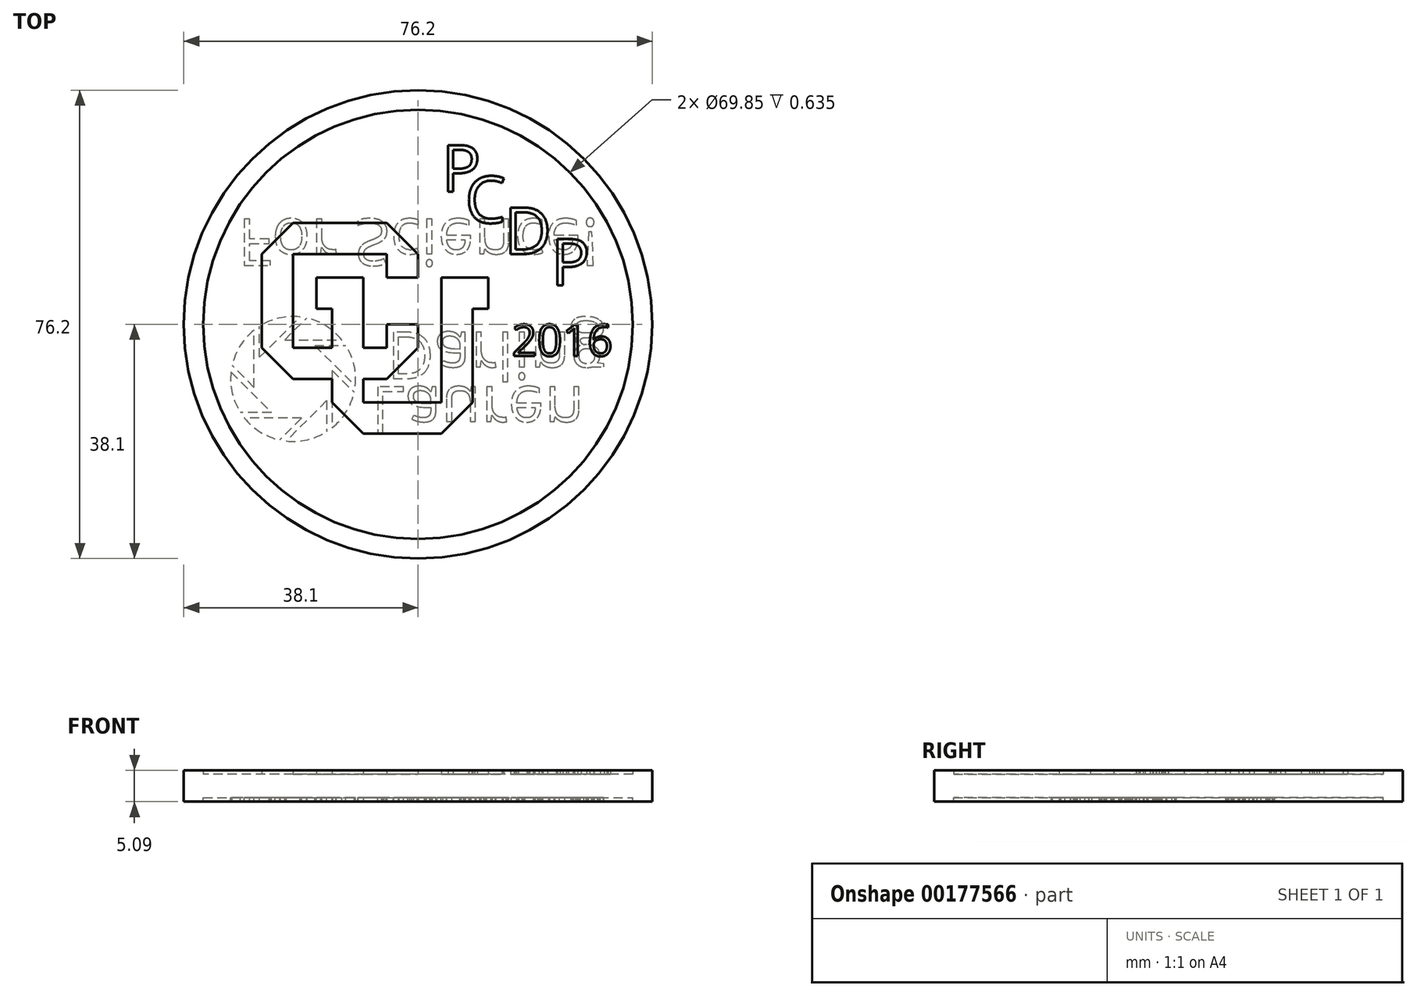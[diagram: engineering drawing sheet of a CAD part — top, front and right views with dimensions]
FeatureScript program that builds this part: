
annotation { "Feature Type Name" : "Feature", "Feature Type Description" : "" }
export const myFeature = defineFeature(function(context is Context, id is Id, definition is map)
    precondition{}
    {
        {
            var Q0;
            Q0=qCreatedBy(makeId("Top.planeOp"),FACE);
            var sketch = newSketch(context, id + "F0", { "sketchPlane" : qUnion([Q0])});
            skCircle(sketch, "E0", {"center": v(0, 0) * mm, "radius": 38.1 * mm});
            skSolve(sketch);
        }
        {
            var Q0;
            Q0 = qSketchRegion(id + "F0", true);
            extrude(context, id + "F1", {"entities" : qUnion([Q0]), "depth" : 3.8 * mm});
        }
        {
            var Q0;
            Q0=makeQuery(id+"F1.opExtrude","CAP_FACE",FACE,{"disambiguationData":[OSD([sQuery(id+"F0.wireOp",EDGE,"E0")])],"isStart":false});
            var sketch = newSketch(context, id + "F2", { "sketchPlane" : qUnion([Q0])});
            skCircle(sketch, "E1", {"center": v(0, 0) * mm, "radius": 38.1 * mm});
            skCircle(sketch, "E2", {"center": v(0, 0) * mm, "radius": 34.93 * mm});
            skLineSegment(sketch, "E3", {"start": v(0, 0) * mm, "end": v(0, -3.81) * mm});
            skLineSegment(sketch, "E4", {"start": v(0, -3.81) * mm, "end": v(-5.08, -8.9) * mm});
            skLineSegment(sketch, "E5", {"start": v(-5.08, -8.89) * mm, "end": v(-8.9, -8.89) * mm});
            skLineSegment(sketch, "E6", {"start": v(-20.32, -8.9) * mm, "end": v(-25.4, -3.8) * mm});
            skLineSegment(sketch, "E7", {"start": v(-25.4, -3.81) * mm, "end": v(-25.4, 11.43) * mm});
            skLineSegment(sketch, "E8", {"start": v(-25.4, 11.43) * mm, "end": v(-20.32, 16.51) * mm});
            skLineSegment(sketch, "E9", {"start": v(-20.32, 16.5) * mm, "end": v(-5.08, 16.51) * mm});
            skLineSegment(sketch, "E10", {"start": v(-5.08, 16.51) * mm, "end": v(0, 11.43) * mm});
            skLineSegment(sketch, "E11", {"start": v(0, 11.43) * mm, "end": v(0, 7.62) * mm});
            skLineSegment(sketch, "E12", {"start": v(0, 7.62) * mm, "end": v(-5.08, 7.62) * mm});
            skLineSegment(sketch, "E13", {"start": v(-5.08, 7.62) * mm, "end": v(-5.08, 11.43) * mm});
            skLineSegment(sketch, "E14", {"start": v(-5.08, 11.43) * mm, "end": v(-20.32, 11.43) * mm});
            skLineSegment(sketch, "E15", {"start": v(-20.32, 11.43) * mm, "end": v(-20.32, -3.81) * mm});
            skLineSegment(sketch, "E16", {"start": v(-20.32, -3.81) * mm, "end": v(-13.97, -3.81) * mm});
            skLineSegment(sketch, "E17", {"start": v(-5.08, -3.81) * mm, "end": v(-5.08, 0) * mm});
            skLineSegment(sketch, "E18", {"start": v(-5.08, 0) * mm, "end": v(0, 0) * mm});
            skLineSegment(sketch, "E19", {"start": v(-8.9, -3.81) * mm, "end": v(-8.9, 7.62) * mm});
            skLineSegment(sketch, "E20", {"start": v(-8.9, 7.62) * mm, "end": v(-16.51, 7.62) * mm});
            skLineSegment(sketch, "E21", {"start": v(-16.51, 7.62) * mm, "end": v(-16.51, 2.54) * mm});
            skLineSegment(sketch, "E22", {"start": v(-16.51, 2.54) * mm, "end": v(-13.97, 2.54) * mm});
            skLineSegment(sketch, "E23", {"start": v(-13.97, 2.54) * mm, "end": v(-13.97, -3.81) * mm});
            skLineSegment(sketch, "E24", {"start": v(-13.97, -8.9) * mm, "end": v(-13.97, -12.7) * mm});
            skLineSegment(sketch, "E25", {"start": v(-13.97, -12.7) * mm, "end": v(-8.89, -17.78) * mm});
            skLineSegment(sketch, "E26", {"start": v(-8.9, -17.78) * mm, "end": v(3.8, -17.78) * mm});
            skLineSegment(sketch, "E27", {"start": v(3.8, -17.78) * mm, "end": v(8.9, -12.7) * mm});
            skLineSegment(sketch, "E28", {"start": v(8.9, -12.7) * mm, "end": v(8.9, 2.54) * mm});
            skLineSegment(sketch, "E29", {"start": v(8.9, 2.54) * mm, "end": v(11.43, 2.54) * mm});
            skLineSegment(sketch, "E30", {"start": v(11.43, 2.54) * mm, "end": v(11.43, 7.62) * mm});
            skLineSegment(sketch, "E31", {"start": v(11.43, 7.62) * mm, "end": v(3.8, 7.62) * mm});
            skLineSegment(sketch, "E32", {"start": v(3.8, 7.62) * mm, "end": v(3.81, -12.7) * mm});
            skLineSegment(sketch, "E33", {"start": v(3.81, -12.7) * mm, "end": v(-8.9, -12.7) * mm});
            skLineSegment(sketch, "E34", {"start": v(-8.9, -12.7) * mm, "end": v(-8.9, -8.9) * mm});
            skLineSegment(sketch, "E35.trimOffspring", {"start": v(-8.9, -3.8) * mm, "end": v(-5.08, -3.8) * mm});
            skLineSegment(sketch, "E36.trimOffspring", {"start": v(-13.97, -8.9) * mm, "end": v(-20.32, -8.9) * mm});
            skText(sketch, "E37", { "text": "P", "fontName": "OpenSans-Regular.ttf"});
            skText(sketch, "E38", { "text": "C", "fontName": "OpenSans-Regular.ttf"});
            skText(sketch, "E39", { "text": "D", "fontName": "OpenSans-Regular.ttf"});
            skText(sketch, "E40", { "text": "P\n", "fontName": "OpenSans-Regular.ttf"});
            skText(sketch, "E41", { "text": "2016", "fontName": "OpenSans-Regular.ttf"});
            const initialGuessF2  = {"E37": [0.0038, 0.0216, 1, 0, 0.00762], "E38": [0.00762, 0.01651, 1, 0, 0.00762], "E39": [0.01397, 0.01143, 1, 0, 0.00762], "E40": [0.0216, 0.00635, 1, 0, 0.00762], "E41": [0.01524, -0.00516, 1, 0, 0.00516]};
            skSetInitialGuess(sketch, initialGuessF2);
            skSolve(sketch);
        }
        {
            var Q0;
            Q0 = qSketchRegion(id + "F2", true);
            var Q1;
            Q1=makeQuery(id+"F2.imprint","IMPRINT",FACE,{"disambiguationData":[TD([[makeQuery(id+"F2.imprint","IMPRINT",EDGE,{"derivedFrom":sQuery(id+"F2.wireOp",EDGE,"E39.sketch_text.stroke-0")}),-1.0]])]});
            var Q2;
            Q2=makeQuery(id+"F2.imprint","IMPRINT",FACE,{"disambiguationData":[TD([[makeQuery(id+"F2.imprint","IMPRINT",EDGE,{"derivedFrom":sQuery(id+"F2.wireOp",EDGE,"E40.sketch_text.stroke-0")}),-1.0]])]});
            var Q3;
            Q3=makeQuery(id+"F2.imprint","IMPRINT",FACE,{"disambiguationData":[TD([[makeQuery(id+"F2.imprint","IMPRINT",EDGE,{"derivedFrom":sQuery(id+"F2.wireOp",EDGE,"E38.sketch_text.stroke-0")}),-1.0]])]});
            var Q4;
            Q4=makeQuery(id+"F2.imprint","IMPRINT",FACE,{"disambiguationData":[TD([[makeQuery(id+"F2.imprint","IMPRINT",EDGE,{"derivedFrom":sQuery(id+"F2.wireOp",EDGE,"E37.sketch_text.stroke-0")}),-1.0]])]});
            var Q5;
            Q5=makeQuery(id+"F2.imprint","IMPRINT",FACE,{"disambiguationData":[TD([[makeQuery(id+"F2.imprint","IMPRINT",EDGE,{"derivedFrom":sQuery(id+"F2.wireOp",EDGE,"E41.sketch_text.stroke-0")}),-1.0]])]});
            var Q6;
            Q6=makeQuery(id+"F2.imprint","IMPRINT",FACE,{"disambiguationData":[TD([[makeQuery(id+"F2.imprint","IMPRINT",EDGE,{"derivedFrom":sQuery(id+"F2.wireOp",EDGE,"E41.sketch_text.stroke-20")}),-1.0]])]});
            var Q7;
            Q7=makeQuery(id+"F2.imprint","IMPRINT",FACE,{"disambiguationData":[TD([[makeQuery(id+"F2.imprint","IMPRINT",EDGE,{"derivedFrom":sQuery(id+"F2.wireOp",EDGE,"E41.sketch_text.stroke-36")}),-1.0]])]});
            var Q8;
            Q8=makeQuery(id+"F2.imprint","IMPRINT",FACE,{"disambiguationData":[TD([[makeQuery(id+"F2.imprint","IMPRINT",EDGE,{"derivedFrom":sQuery(id+"F2.wireOp",EDGE,"E41.sketch_text.stroke-45")}),-1.0]])]});
            var Q9;
            Q9=makeQuery(id+"F2.imprint","IMPRINT",FACE,{"disambiguationData":[TD([[makeQuery(id+"F2.imprint","IMPRINT",EDGE,{"derivedFrom":sQuery(id+"F2.wireOp",EDGE,"E3")}),-1.0]])]});
            extrude(context, id + "F3", {"entities" : qUnion([Q0, Q1, Q2, Q3, Q4, Q5, Q6, Q7, Q8, Q9]), "operationType" : NewBodyOperationType.ADD, "depth" : 0.64 * mm});
        }
        {
            var Q0;
            Q0=makeQuery(id+"F1.opExtrude","CAP_FACE",FACE,{"disambiguationData":[OSD([sQuery(id+"F0.wireOp",EDGE,"E0")])],"isStart":true});
            var sketch = newSketch(context, id + "F4", { "sketchPlane" : qUnion([Q0])});
            skCircle(sketch, "E42", {"center": v(0, 0) * mm, "radius": 38.1 * mm});
            skCircle(sketch, "E43", {"center": v(0, 0) * mm, "radius": 34.93 * mm});
            skText(sketch, "E44", { "text": "Lauren\n", "fontName": "OpenSans-Regular.ttf"});
            skText(sketch, "E45", { "text": "Darling", "fontName": "OpenSans-Regular.ttf"});
            skArc(sketch, "E46", {"start": v(-28.89, 14.35) * mm, "mid": v(-30.22, 11.2) * mm, "end": v(-30.42, 7.77) * mm});
            skLineSegment(sketch, "E47.0", {"start": v(-22.95, 15.24) * mm, "end": v(-18.95, 15.24) * mm});
            skLineSegment(sketch, "E47.1", {"start": v(-17.69, 15.24) * mm, "end": v(-14.86, 12.4) * mm});
            skLineSegment(sketch, "E47.2", {"start": v(-13.97, 8.89) * mm, "end": v(-13.97, 7.52) * mm});
            skLineSegment(sketch, "E47.3", {"start": v(-13.97, 6.26) * mm, "end": v(-16.8, 3.43) * mm});
            skLineSegment(sketch, "E47.4", {"start": v(-17.69, 2.54) * mm, "end": v(-21.7, 2.54) * mm});
            skLineSegment(sketch, "E47.5", {"start": v(-22.95, 2.54) * mm, "end": v(-25.78, 5.37) * mm});
            skLineSegment(sketch, "E47.6", {"start": v(-26.67, 6.26) * mm, "end": v(-26.67, 10.26) * mm});
            skLineSegment(sketch, "E47.7", {"start": v(-26.67, 11.52) * mm, "end": v(-23.84, 14.35) * mm});
            skPoint(sketch, "E47.0.midPoint", {"position": v(-20.32, 15.24) * mm});
            skLineSegment(sketch, "E48", {"start": v(-13.97, 11.52) * mm, "end": v(-13.97, 16.82) * mm});
            skLineSegment(sketch, "E49.trimOffspring", {"start": v(-14.86, 12.4) * mm, "end": v(-14.86, 17.46) * mm});
            skLineSegment(sketch, "E50.1.0", {"start": v(-18.95, 15.24) * mm, "end": v(-22.52, 18.8) * mm});
            skLineSegment(sketch, "E50.1.1", {"start": v(-17.69, 15.24) * mm, "end": v(-21.44, 18.99) * mm});
            skLineSegment(sketch, "E50.2.0", {"start": v(-23.84, 14.35) * mm, "end": v(-28.89, 14.35) * mm});
            skLineSegment(sketch, "E50.2.1", {"start": v(-22.95, 15.24) * mm, "end": v(-28.25, 15.24) * mm});
            skLineSegment(sketch, "E50.3.0", {"start": v(-26.67, 10.26) * mm, "end": v(-30.24, 6.7) * mm});
            skLineSegment(sketch, "E50.3.1", {"start": v(-26.67, 11.52) * mm, "end": v(-30.42, 7.77) * mm});
            skLineSegment(sketch, "E50.4.0", {"start": v(-25.78, 5.37) * mm, "end": v(-25.78, 0.32) * mm});
            skLineSegment(sketch, "E50.4.1", {"start": v(-26.67, 6.26) * mm, "end": v(-26.67, 0.96) * mm});
            skLineSegment(sketch, "E50.5.0", {"start": v(-21.7, 2.54) * mm, "end": v(-18.12, -1.03) * mm});
            skLineSegment(sketch, "E50.5.1", {"start": v(-22.95, 2.54) * mm, "end": v(-19.2, -1.2) * mm});
            skLineSegment(sketch, "E50.6.0", {"start": v(-16.8, 3.43) * mm, "end": v(-11.75, 3.43) * mm});
            skLineSegment(sketch, "E50.6.1", {"start": v(-17.69, 2.54) * mm, "end": v(-12.39, 2.54) * mm});
            skLineSegment(sketch, "E50.7.0", {"start": v(-13.97, 7.52) * mm, "end": v(-10.4, 11.09) * mm});
            skLineSegment(sketch, "E50.7.1", {"start": v(-13.97, 6.26) * mm, "end": v(-10.22, 10) * mm});
            skLineSegment(sketch, "E51", {"start": v(-13.97, 8.89) * mm, "end": v(-13.97, 11.52) * mm});
            skArc(sketch, "E52.trimOffspring", {"start": v(-22.52, 18.8) * mm, "mid": v(-25.69, 17.52) * mm, "end": v(-28.25, 15.24) * mm});
            skArc(sketch, "E53.trimOffspring", {"start": v(-14.86, 17.46) * mm, "mid": v(-18.02, 18.79) * mm, "end": v(-21.44, 18.99) * mm});
            skArc(sketch, "E54.trimOffspring", {"start": v(-10.4, 11.09) * mm, "mid": v(-11.7, 14.26) * mm, "end": v(-13.97, 16.82) * mm});
            skArc(sketch, "E55.trimOffspring", {"start": v(-11.75, 3.43) * mm, "mid": v(-10.42, 6.59) * mm, "end": v(-10.22, 10) * mm});
            skArc(sketch, "E56.trimOffspring", {"start": v(-25.78, 0.32) * mm, "mid": v(-22.62, -1) * mm, "end": v(-19.2, -1.2) * mm});
            skArc(sketch, "E57.trimOffspring", {"start": v(-30.24, 6.7) * mm, "mid": v(-28.95, 3.52) * mm, "end": v(-26.67, 0.96) * mm});
            skArc(sketch, "E58.trimOffspring", {"start": v(-18.12, -1.03) * mm, "mid": v(-14.95, 0.26) * mm, "end": v(-12.39, 2.54) * mm});
            skText(sketch, "E59", { "text": "For Science!", "fontName": "OpenSans-Regular.ttf"});
            const initialGuessF4  = {"E44": [-0.00762, 0.01016, 1, 0, 0.00762], "E45": [-0.00508, 0.00127, 1, 0, 0.00762], "E59": [-0.02929, -0.01715, 1, 0, 0.00762]};
            skSetInitialGuess(sketch, initialGuessF4);
            skSolve(sketch);
        }
        {
            var Q0;
            Q0=makeQuery(id+"F4.imprint","IMPRINT",FACE,{"disambiguationData":[TD([[makeQuery(id+"F4.imprint","IMPRINT",EDGE,{"derivedFrom":sQuery(id+"F4.wireOp",EDGE,"E45.sketch_text.stroke-70")}),-1.0]])]});
            var Q1;
            Q1=makeQuery(id+"F4.imprint","IMPRINT",FACE,{"disambiguationData":[TD([[makeQuery(id+"F4.imprint","IMPRINT",EDGE,{"derivedFrom":sQuery(id+"F4.wireOp",EDGE,"E45.sketch_text.stroke-58")}),-1.0]])]});
            var Q2;
            Q2=makeQuery(id+"F4.imprint","IMPRINT",FACE,{"disambiguationData":[TD([[makeQuery(id+"F4.imprint","IMPRINT",EDGE,{"derivedFrom":sQuery(id+"F4.wireOp",EDGE,"E45.sketch_text.stroke-62")}),-1.0]])]});
            var Q3;
            Q3=makeQuery(id+"F4.imprint","IMPRINT",FACE,{"disambiguationData":[TD([[makeQuery(id+"F4.imprint","IMPRINT",EDGE,{"derivedFrom":sQuery(id+"F4.wireOp",EDGE,"E45.sketch_text.stroke-54")}),-1.0]])]});
            var Q4;
            Q4=makeQuery(id+"F4.imprint","IMPRINT",FACE,{"disambiguationData":[TD([[makeQuery(id+"F4.imprint","IMPRINT",EDGE,{"derivedFrom":sQuery(id+"F4.wireOp",EDGE,"E45.sketch_text.stroke-41")}),-1.0]])]});
            var Q5;
            Q5=makeQuery(id+"F4.imprint","IMPRINT",FACE,{"disambiguationData":[TD([[makeQuery(id+"F4.imprint","IMPRINT",EDGE,{"derivedFrom":sQuery(id+"F4.wireOp",EDGE,"E45.sketch_text.stroke-14")}),-1.0]])]});
            var Q6;
            Q6=makeQuery(id+"F4.imprint","IMPRINT",FACE,{"disambiguationData":[TD([[makeQuery(id+"F4.imprint","IMPRINT",EDGE,{"derivedFrom":sQuery(id+"F4.wireOp",EDGE,"E45.sketch_text.stroke-0")}),-1.0]])]});
            var Q7;
            Q7=makeQuery(id+"F4.imprint","IMPRINT",FACE,{"disambiguationData":[TD([[makeQuery(id+"F4.imprint","IMPRINT",EDGE,{"derivedFrom":sQuery(id+"F4.wireOp",EDGE,"E45.sketch_text.stroke-87")}),-1.0]])]});
            var Q8;
            Q8=makeQuery(id+"F4.imprint","IMPRINT",FACE,{"disambiguationData":[TD([[makeQuery(id+"F4.imprint","IMPRINT",EDGE,{"derivedFrom":sQuery(id+"F4.wireOp",EDGE,"E44.sketch_text.stroke-0")}),-1.0]])]});
            var Q9;
            Q9=makeQuery(id+"F4.imprint","IMPRINT",FACE,{"disambiguationData":[TD([[makeQuery(id+"F4.imprint","IMPRINT",EDGE,{"derivedFrom":sQuery(id+"F4.wireOp",EDGE,"E44.sketch_text.stroke-6")}),-1.0]])]});
            var Q10;
            Q10=makeQuery(id+"F4.imprint","IMPRINT",FACE,{"disambiguationData":[TD([[makeQuery(id+"F4.imprint","IMPRINT",EDGE,{"derivedFrom":sQuery(id+"F4.wireOp",EDGE,"E44.sketch_text.stroke-33")}),-1.0]])]});
            var Q11;
            Q11=makeQuery(id+"F4.imprint","IMPRINT",FACE,{"disambiguationData":[TD([[makeQuery(id+"F4.imprint","IMPRINT",EDGE,{"derivedFrom":sQuery(id+"F4.wireOp",EDGE,"E44.sketch_text.stroke-50")}),-1.0]])]});
            var Q12;
            Q12=makeQuery(id+"F4.imprint","IMPRINT",FACE,{"disambiguationData":[TD([[makeQuery(id+"F4.imprint","IMPRINT",EDGE,{"derivedFrom":sQuery(id+"F4.wireOp",EDGE,"E44.sketch_text.stroke-63")}),-1.0]])]});
            var Q13;
            Q13=makeQuery(id+"F4.imprint","IMPRINT",FACE,{"disambiguationData":[TD([[makeQuery(id+"F4.imprint","IMPRINT",EDGE,{"derivedFrom":sQuery(id+"F4.wireOp",EDGE,"E44.sketch_text.stroke-82")}),-1.0]])]});
            var Q14;
            Q14=makeQuery(id+"F4.imprint","IMPRINT",FACE,{"disambiguationData":[TD([[makeQuery(id+"F4.imprint","IMPRINT",EDGE,{"derivedFrom":sQuery(id+"F4.wireOp",EDGE,"E42")}),-1.0]])]});
            var Q15;
            Q15=makeQuery(id+"F4.imprint","IMPRINT",FACE,{"disambiguationData":[TD([[makeQuery(id+"F4.imprint","IMPRINT",EDGE,{"derivedFrom":sQuery(id+"F4.wireOp",EDGE,"E47.0")}),1.0]])]});
            var Q16;
            Q16=makeQuery(id+"F4.imprint","IMPRINT",FACE,{"disambiguationData":[TD([[makeQuery(id+"F4.imprint","IMPRINT",EDGE,{"derivedFrom":sQuery(id+"F4.wireOp",EDGE,"E47.1")}),1.0]])]});
            var Q17;
            Q17=makeQuery(id+"F4.imprint","IMPRINT",FACE,{"disambiguationData":[TD([[makeQuery(id+"F4.imprint","IMPRINT",EDGE,{"derivedFrom":sQuery(id+"F4.wireOp",EDGE,"E47.2")}),1.0]])]});
            var Q18;
            Q18=makeQuery(id+"F4.imprint","IMPRINT",FACE,{"disambiguationData":[TD([[makeQuery(id+"F4.imprint","IMPRINT",EDGE,{"derivedFrom":sQuery(id+"F4.wireOp",EDGE,"E47.3")}),1.0]])]});
            var Q19;
            Q19=makeQuery(id+"F4.imprint","IMPRINT",FACE,{"disambiguationData":[TD([[makeQuery(id+"F4.imprint","IMPRINT",EDGE,{"derivedFrom":sQuery(id+"F4.wireOp",EDGE,"E47.4")}),1.0]])]});
            var Q20;
            Q20=makeQuery(id+"F4.imprint","IMPRINT",FACE,{"disambiguationData":[TD([[makeQuery(id+"F4.imprint","IMPRINT",EDGE,{"derivedFrom":sQuery(id+"F4.wireOp",EDGE,"E47.5")}),1.0]])]});
            var Q21;
            Q21=makeQuery(id+"F4.imprint","IMPRINT",FACE,{"disambiguationData":[TD([[makeQuery(id+"F4.imprint","IMPRINT",EDGE,{"derivedFrom":sQuery(id+"F4.wireOp",EDGE,"E47.6")}),1.0]])]});
            var Q22;
            Q22=makeQuery(id+"F4.imprint","IMPRINT",FACE,{"disambiguationData":[TD([[makeQuery(id+"F4.imprint","IMPRINT",EDGE,{"derivedFrom":sQuery(id+"F4.wireOp",EDGE,"E46")}),1.0]])]});
            var Q23;
            Q23=makeQuery(id+"F4.imprint","IMPRINT",FACE,{"disambiguationData":[TD([[makeQuery(id+"F4.imprint","IMPRINT",EDGE,{"derivedFrom":sQuery(id+"F4.wireOp",EDGE,"E59.sketch_text.stroke-0")}),-1.0]])]});
            var Q24;
            Q24=makeQuery(id+"F4.imprint","IMPRINT",FACE,{"disambiguationData":[TD([[makeQuery(id+"F4.imprint","IMPRINT",EDGE,{"derivedFrom":sQuery(id+"F4.wireOp",EDGE,"E59.sketch_text.stroke-10")}),-1.0]])]});
            var Q25;
            Q25=makeQuery(id+"F4.imprint","IMPRINT",FACE,{"disambiguationData":[TD([[makeQuery(id+"F4.imprint","IMPRINT",EDGE,{"derivedFrom":sQuery(id+"F4.wireOp",EDGE,"E59.sketch_text.stroke-27")}),-1.0]])]});
            var Q26;
            Q26=makeQuery(id+"F4.imprint","IMPRINT",FACE,{"disambiguationData":[TD([[makeQuery(id+"F4.imprint","IMPRINT",EDGE,{"derivedFrom":sQuery(id+"F4.wireOp",EDGE,"E59.sketch_text.stroke-65")}),-1.0]])]});
            var Q27;
            Q27=makeQuery(id+"F4.imprint","IMPRINT",FACE,{"disambiguationData":[TD([[makeQuery(id+"F4.imprint","IMPRINT",EDGE,{"derivedFrom":sQuery(id+"F4.wireOp",EDGE,"E59.sketch_text.stroke-40")}),-1.0]])]});
            var Q28;
            Q28=makeQuery(id+"F4.imprint","IMPRINT",FACE,{"disambiguationData":[TD([[makeQuery(id+"F4.imprint","IMPRINT",EDGE,{"derivedFrom":sQuery(id+"F4.wireOp",EDGE,"E59.sketch_text.stroke-80")}),-1.0]])]});
            var Q29;
            Q29=makeQuery(id+"F4.imprint","IMPRINT",FACE,{"disambiguationData":[TD([[makeQuery(id+"F4.imprint","IMPRINT",EDGE,{"derivedFrom":sQuery(id+"F4.wireOp",EDGE,"E59.sketch_text.stroke-84")}),-1.0]])]});
            var Q30;
            Q30=makeQuery(id+"F4.imprint","IMPRINT",FACE,{"disambiguationData":[TD([[makeQuery(id+"F4.imprint","IMPRINT",EDGE,{"derivedFrom":sQuery(id+"F4.wireOp",EDGE,"E59.sketch_text.stroke-92")}),-1.0]])]});
            var Q31;
            Q31=makeQuery(id+"F4.imprint","IMPRINT",FACE,{"disambiguationData":[TD([[makeQuery(id+"F4.imprint","IMPRINT",EDGE,{"derivedFrom":sQuery(id+"F4.wireOp",EDGE,"E59.sketch_text.stroke-111")}),-1.0]])]});
            var Q32;
            Q32=makeQuery(id+"F4.imprint","IMPRINT",FACE,{"disambiguationData":[TD([[makeQuery(id+"F4.imprint","IMPRINT",EDGE,{"derivedFrom":sQuery(id+"F4.wireOp",EDGE,"E59.sketch_text.stroke-128")}),-1.0]])]});
            var Q33;
            Q33=makeQuery(id+"F4.imprint","IMPRINT",FACE,{"disambiguationData":[TD([[makeQuery(id+"F4.imprint","IMPRINT",EDGE,{"derivedFrom":sQuery(id+"F4.wireOp",EDGE,"E59.sketch_text.stroke-143")}),-1.0]])]});
            var Q34;
            Q34=makeQuery(id+"F4.imprint","IMPRINT",FACE,{"disambiguationData":[TD([[makeQuery(id+"F4.imprint","IMPRINT",EDGE,{"derivedFrom":sQuery(id+"F4.wireOp",EDGE,"E59.sketch_text.stroke-162")}),-1.0]])]});
            var Q35;
            Q35=makeQuery(id+"F4.imprint","IMPRINT",FACE,{"disambiguationData":[TD([[makeQuery(id+"F4.imprint","IMPRINT",EDGE,{"derivedFrom":sQuery(id+"F4.wireOp",EDGE,"E59.sketch_text.stroke-166")}),-1.0]])]});
            extrude(context, id + "F5", {"entities" : qUnion([Q0, Q1, Q2, Q3, Q4, Q5, Q6, Q7, Q8, Q9, Q10, Q11, Q12, Q13, Q14, Q15, Q16, Q17, Q18, Q19, Q20, Q21, Q22, Q23, Q24, Q25, Q26, Q27, Q28, Q29, Q30, Q31, Q32, Q33, Q34, Q35]), "operationType" : NewBodyOperationType.ADD, "depth" : 0.64 * mm});
        }
    });
